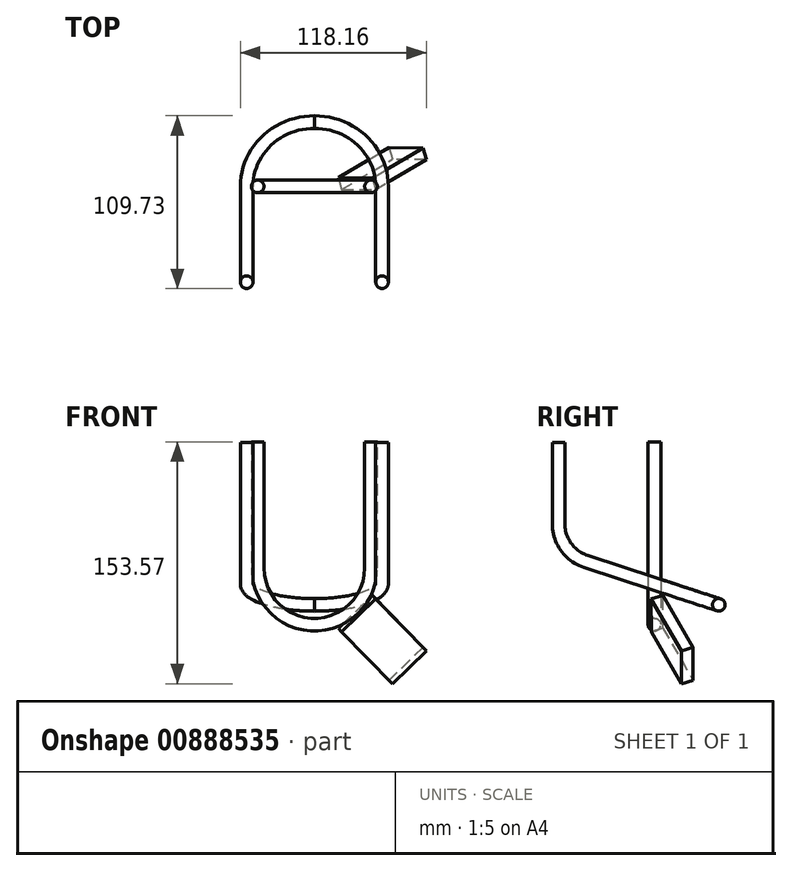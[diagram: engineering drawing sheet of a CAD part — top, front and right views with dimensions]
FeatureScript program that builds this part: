
annotation { "Feature Type Name" : "Feature", "Feature Type Description" : "" }
export const myFeature = defineFeature(function(context is Context, id is Id, definition is map)
    precondition{}
    {
        {
            var Q0;
            Q0=qCreatedBy(makeId("Front.planeOp"),FACE);
            var sketch = newSketch(context, id + "F0", { "sketchPlane" : qUnion([Q0])});
            skLineSegment(sketch, "E0.0", {"start": v(-15, 25) * mm, "end": v(15, 25) * mm});
            skLineSegment(sketch, "E1.0.0", {"start": v(-15, 25) * mm, "end": v(-15, -25) * mm, "construction": true});
            skLineSegment(sketch, "E1.0.1", {"start": v(-15, -25) * mm, "end": v(15, -25) * mm, "construction": true});
            skLineSegment(sketch, "E1.0.2", {"start": v(15, -25) * mm, "end": v(15, 25) * mm, "construction": true});
            skLineSegment(sketch, "E1.0.3", {"start": v(15, 25) * mm, "end": v(-15, 25) * mm, "construction": true});
            skLineSegment(sketch, "E2", {"start": v(0, 25) * mm, "end": v(0, 25) * mm});
            skLineSegment(sketch, "E3", {"start": v(-40, 65) * mm, "end": v(-40, 145) * mm});
            skPoint(sketch, "E4.visualSharp", {"position": v(-40, 25) * mm});
            skArc(sketch, "E4.filletArc", {"start": v(-40, 65) * mm, "mid": v(-28.28, 36.72) * mm, "end": v(0, 25) * mm});
            skArc(sketch, "E5.MirrorCS", {"start": v(40, 65) * mm, "mid": v(28.28, 36.72) * mm, "end": v(0, 25) * mm});
            skLineSegment(sketch, "E6.MirrorCS", {"start": v(40, 65) * mm, "end": v(40, 145) * mm});
            skSolve(sketch);
        }
        {
            var Q0;
            Q0=sQuery(id+"F0.wireOp",VERTEX,"E3.end");
            var Q1;
            Q1=sQuery(id+"F0.wireOp",EDGE,"E3");
            cPlane(context, id + "F1", {"entities" : qUnion([Q0, Q1]), "cplaneType" : CPlaneType.LINE_POINT, "offset" : 25 * mm, "width" : 150 * mm, "height" : 150 * mm});
        }
        {
            var Q0;
            Q0=qCreatedBy(id+"F1.planeOp",FACE);
            var sketch = newSketch(context, id + "F2", { "sketchPlane" : qUnion([Q0])});
            skCircle(sketch, "E7", {"center": v(-36, 0) * mm, "radius": 4 * mm});
            skSolve(sketch);
        }
        {
            var Q0;
            Q0=makeQuery(id+"F2.imprint","IMPRINT",FACE,{"disambiguationData":[TD([[makeQuery(id+"F2.imprint","IMPRINT",EDGE,{"derivedFrom":sQuery(id+"F2.wireOp",EDGE,"E7")}),1.0]])]});
            var Q1;
            Q1=sQuery(id+"F0.wireOp",EDGE,"E3");
            var Q2;
            Q2=sQuery(id+"F0.wireOp",EDGE,"E4.filletArc");
            var Q3;
            Q3=sQuery(id+"F0.wireOp",EDGE,"E5.MirrorCS");
            var Q4;
            Q4=sQuery(id+"F0.wireOp",EDGE,"E6.MirrorCS");
            sweep(context, id + "F3", {"profiles" : qUnion([Q0]), "path" : qUnion([Q1, Q2, Q3, Q4])});
        }
        {
            var Q0;
            Q0=qCreatedBy(makeId("Top.planeOp"),FACE);
            cPlane(context, id + "F4", {"entities" : qUnion([Q0]), "cplaneType" : CPlaneType.OFFSET, "offset" : 65 * mm, "width" : 150 * mm, "height" : 150 * mm});
        }
        {
            var Q0;
            Q0=qCreatedBy(id+"F4.planeOp",FACE);
            var sketch = newSketch(context, id + "F5", { "sketchPlane" : qUnion([Q0])});
            skLineSegment(sketch, "E8", {"start": v(0, -72.53) * mm, "end": v(0, 68.69) * mm});
            skLineSegment(sketch, "E9", {"start": v(-63.07, 0) * mm, "end": v(67.14, 0) * mm});
            skSolve(sketch);
        }
        {
            var Q0;
            Q0=qCreatedBy(makeId("Right.planeOp"),FACE);
            cPlane(context, id + "F6", {"entities" : qUnion([Q0]), "cplaneType" : CPlaneType.OFFSET, "offset" : 43 * mm, "width" : 150 * mm, "height" : 150 * mm});
        }
        {
            var Q0;
            Q0=qCreatedBy(id+"F6.planeOp",FACE);
            var sketch = newSketch(context, id + "F7", { "sketchPlane" : qUnion([Q0])});
            skLineSegment(sketch, "E10", {"start": v(-60.85, 144.59) * mm, "end": v(-60.85, 92.9) * mm});
            skLineSegment(sketch, "E11", {"start": v(-43.61, 69.13) * mm, "end": v(0, 54.89) * mm});
            skPoint(sketch, "E12.visualSharp", {"position": v(-60.85, 74.76) * mm});
            skArc(sketch, "E13.filletArc", {"start": v(-60.85, 92.9) * mm, "mid": v(-56.09, 78.22) * mm, "end": v(-43.61, 69.13) * mm});
            skSolve(sketch);
        }
        {
            var Q0;
            Q0=sQuery(id+"F7.wireOp",VERTEX,"E10.start");
            var Q1;
            Q1=sQuery(id+"F7.wireOp",EDGE,"E10");
            cPlane(context, id + "F8", {"entities" : qUnion([Q0, Q1]), "cplaneType" : CPlaneType.LINE_POINT, "offset" : 25 * mm, "width" : 150 * mm, "height" : 150 * mm});
        }
        {
            var Q0;
            Q0=qCreatedBy(id+"F8.planeOp",FACE);
            var sketch = newSketch(context, id + "F9", { "sketchPlane" : qUnion([Q0])});
            skPoint(sketch, "E14.0", {"position": v(43, 60.85) * mm});
            skCircle(sketch, "E15", {"center": v(43, 60.85) * mm, "radius": 4 * mm});
            skSolve(sketch);
        }
        {
            var Q0;
            Q0=makeQuery(id+"F9.imprint","IMPRINT",FACE,{"disambiguationData":[TD([[makeQuery(id+"F9.imprint","IMPRINT",EDGE,{"derivedFrom":sQuery(id+"F9.wireOp",EDGE,"E15")}),1.0]])]});
            var Q1;
            Q1=sQuery(id+"F7.wireOp",EDGE,"E10");
            var Q2;
            Q2=sQuery(id+"F7.wireOp",EDGE,"E13.filletArc");
            var Q3;
            Q3=sQuery(id+"F7.wireOp",EDGE,"E11");
            sweep(context, id + "F10", {"profiles" : qUnion([Q0]), "path" : qUnion([Q1, Q2, Q3])});
        }
        {
            var Q0;
            Q0=sQuery(id+"F7.wireOp",VERTEX,"E11.end");
            var Q1;
            Q1=sQuery(id+"F7.wireOp",EDGE,"E11");
            cPlane(context, id + "F11", {"entities" : qUnion([Q0, Q1]), "cplaneType" : CPlaneType.LINE_POINT, "offset" : 25 * mm, "width" : 150 * mm, "height" : 150 * mm});
        }
        {
            var Q0;
            Q0=qCreatedBy(id+"F11.planeOp",FACE);
            var sketch = newSketch(context, id + "F12", { "sketchPlane" : qUnion([Q0])});
            skPoint(sketch, "E16.0", {"position": v(-43, 52.17) * mm});
            skLineSegment(sketch, "E17", {"start": v(-82.9, 52.17) * mm, "end": v(5.79, 52.17) * mm});
            skSolve(sketch);
        }
        {
            var Q0;
            Q0=sQuery(id+"F12.wireOp",EDGE,"E17");
            var Q1;
            Q1=sQuery(id+"F7.wireOp",EDGE,"E11");
            cPlane(context, id + "F13", {"entities" : qUnion([Q0, Q1]), "cplaneType" : CPlaneType.LINE_ANGLE, "offset" : 25 * mm, "angle" : 0 * degree, "width" : 150 * mm, "height" : 150 * mm});
        }
        {
            var Q0;
            Q0=qCreatedBy(id+"F13.planeOp",FACE);
            var sketch = newSketch(context, id + "F14", { "sketchPlane" : qUnion([Q0])});
            skPoint(sketch, "E18.0", {"position": v(43, 17.04) * mm});
            skLineSegment(sketch, "E19", {"start": v(43, 17.04) * mm, "end": v(43, 17.04) * mm});
            skLineSegment(sketch, "E20", {"start": v(0, -25.96) * mm, "end": v(0, -25.96) * mm});
            skPoint(sketch, "E21.visualSharp", {"position": v(43, -25.96) * mm});
            skArc(sketch, "E21.filletArc", {"start": v(0, -25.96) * mm, "mid": v(30.4, -13.37) * mm, "end": v(43, 17.04) * mm});
            skSolve(sketch);
        }
        {
            var Q0;
            Q0=makeQuery(id+"F10.opSweep","CAP_FACE",FACE,{"disambiguationData":[OSD([sQuery(id+"F7.wireOp",VERTEX,"E11.end"),sQuery(id+"F9.wireOp",EDGE,"E15")])],"isStart":false});
            var Q1;
            Q1=sQuery(id+"F14.wireOp",EDGE,"E21.filletArc");
            sweep(context, id + "F15", {"operationType" : NewBodyOperationType.ADD, "profiles" : qUnion([Q0]), "path" : qUnion([Q1])});
        }
        {
            var Q0;
            Q0=makeQuery(id+"F10.opSweep","SWEPT_BODY",BODY,{"disambiguationData":[OSD([sQuery(id+"F7.wireOp",EDGE,"E11"),sQuery(id+"F9.wireOp",EDGE,"E15")])]});
            var Q1;
            Q1=qCreatedBy(makeId("Right.planeOp"),FACE);
            mirror(context, id + "F16", {"operationType" : NewBodyOperationType.ADD, "entities" : qUnion([Q0]), "mirrorPlane" : qUnion([Q1])});
        }
        {
            var Q0;
            Q0=qCreatedBy(makeId("Top.planeOp"),FACE);
            cPlane(context, id + "F17", {"entities" : qUnion([Q0]), "cplaneType" : CPlaneType.OFFSET, "offset" : 25 * mm, "width" : 150 * mm, "height" : 150 * mm});
        }
        {
            var Q0;
            Q0=qCreatedBy(id+"F17.planeOp",FACE);
            var sketch = newSketch(context, id + "F18", { "sketchPlane" : qUnion([Q0])});
            skLineSegment(sketch, "E22", {"start": v(106.16, 0) * mm, "end": v(-123.52, 0) * mm});
            skSolve(sketch);
        }
        {
            var Q0;
            Q0=sQuery(id+"F18.wireOp",EDGE,"E22");
            cPlane(context, id + "F19", {"entities" : qUnion([Q0]), "cplaneType" : CPlaneType.LINE_ANGLE, "offset" : 25 * mm, "angle" : 30 * degree, "oppositeDirection" : true, "width" : 150 * mm, "height" : 150 * mm});
        }
        {
            var Q0;
            Q0=qCreatedBy(id+"F19.planeOp",FACE);
            var sketch = newSketch(context, id + "F20", { "sketchPlane" : qUnion([Q0])});
            skFitSpline(sketch, "E23", {"points": [v(40, 56.3) * mm, v(40, 54.12) * mm, v(39.55, 49.79) * mm, v(37.5, 43.44) * mm, v(34.07, 37.43) * mm, v(29.29, 31.99) * mm, v(23.25, 27.37) * mm, v(16.15, 23.84) * mm, v(8.28, 21.62) * mm, v(0, 20.86) * mm, v(-8.28, 21.62) * mm, v(-16.15, 23.84) * mm, v(-23.25, 27.37) * mm, v(-29.29, 31.99) * mm, v(-34.07, 37.43) * mm, v(-37.5, 43.44) * mm, v(-39.55, 49.79) * mm, v(-40, 54.12) * mm, v(-40, 56.3) * mm], "construction": true});
            skLineSegment(sketch, "E24", {"start": v(16.84, 21.73) * mm, "end": v(39.75, 41.09) * mm});
            skLineSegment(sketch, "E25", {"start": v(16.84, 21.73) * mm, "end": v(49.1, -16.47) * mm});
            skLineSegment(sketch, "E26", {"start": v(39.75, 41.09) * mm, "end": v(72.02, 2.9) * mm});
            skLineSegment(sketch, "E27", {"start": v(72.02, 2.9) * mm, "end": v(49.1, -16.47) * mm});
            skSolve(sketch);
        }
        {
            var Q0;
            Q0=makeQuery(id+"F20.imprint","IMPRINT",FACE,{"disambiguationData":[TD([[makeQuery(id+"F20.imprint","IMPRINT",EDGE,{"derivedFrom":sQuery(id+"F20.wireOp",EDGE,"E24")}),-1.0]])]});
            extrude(context, id + "F21", {"entities" : qUnion([Q0]), "oppositeDirection" : true, "depth" : 8 * mm, "offsetDistance" : 25 * mm});
        }
        {
            var Q0;
            Q0=makeQuery(id+"F21.opExtrude","SWEPT_BODY",BODY,{"disambiguationData":[OSD([sQuery(id+"F20.wireOp",EDGE,"E24"),sQuery(id+"F20.wireOp",EDGE,"E25"),sQuery(id+"F20.wireOp",EDGE,"E26"),sQuery(id+"F20.wireOp",EDGE,"E27")])]});
            var Q1;
            Q1=makeQuery(id+"F21.opExtrude","CAP_EDGE",EDGE,{"disambiguationData":[OSD([sQuery(id+"F20.wireOp",EDGE,"E25")])],"isStart":true});
            transform(context, id + "F22", {"entities" : qUnion([Q0]), "transformType" : TransformType.ROTATION, "transformAxis" : qUnion([Q1]), "angle" : 20 * degree, "oppositeDirection" : true, "makeCopy" : false});
        }
        {
            var Q0;
            Q0=makeQuery(id+"F21.opExtrude","SWEPT_BODY",BODY,{"disambiguationData":[OSD([sQuery(id+"F20.wireOp",EDGE,"E24"),sQuery(id+"F20.wireOp",EDGE,"E25"),sQuery(id+"F20.wireOp",EDGE,"E26"),sQuery(id+"F20.wireOp",EDGE,"E27")])]});
            var Q1;
            Q1=makeQuery(id+"F21.opExtrude","SWEPT_EDGE",EDGE,{"disambiguationData":[OSD([sQuery(id+"F20.wireOp",EDGE,"E25"),sQuery(id+"F20.wireOp",EDGE,"E27")])]});
            var Q2;
            Q2=makeQuery(id+"F21.opExtrude","SWEPT_EDGE",EDGE,{"disambiguationData":[OSD([sQuery(id+"F20.wireOp",EDGE,"E25"),sQuery(id+"F20.wireOp",EDGE,"E27")])]});
            transform(context, id + "F23", {"entities" : qUnion([Q0]), "transformType" : TransformType.TRANSLATION_DISTANCE, "transformDirection" : qUnion([Q2]), "distance" : 2 * mm, "makeCopy" : false});
        }
    });
